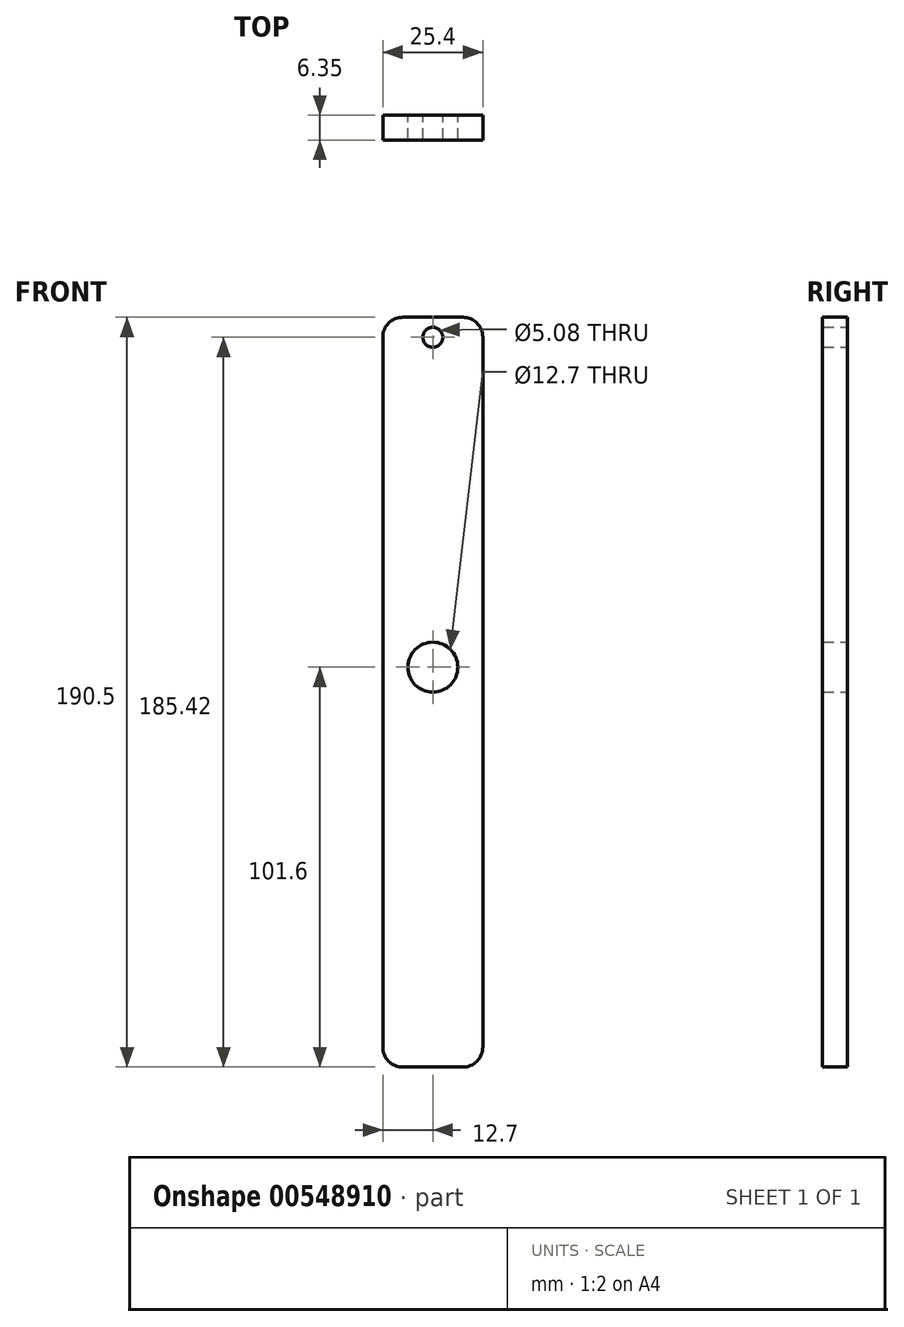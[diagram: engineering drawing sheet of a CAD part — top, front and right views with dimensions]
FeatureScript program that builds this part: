
annotation { "Feature Type Name" : "Feature", "Feature Type Description" : "" }
export const myFeature = defineFeature(function(context is Context, id is Id, definition is map)
    precondition{}
    {
        {
            var Q0;
            Q0=qCreatedBy(makeId("Front.planeOp"),FACE);
            var sketch = newSketch(context, id + "F0", { "sketchPlane" : qUnion([Q0])});
            skLineSegment(sketch, "E0.bottom", {"start": v(7.62, 95.25) * mm, "end": v(-7.62, 95.25) * mm});
            skLineSegment(sketch, "E0.top", {"start": v(7.62, -95.25) * mm, "end": v(-7.62, -95.25) * mm});
            skLineSegment(sketch, "E0.left", {"start": v(12.7, 90.17) * mm, "end": v(12.7, -90.17) * mm});
            skLineSegment(sketch, "E0.right", {"start": v(-12.7, 90.17) * mm, "end": v(-12.7, -90.17) * mm});
            skPoint(sketch, "E0.middle", {"position": v(0, 0) * mm});
            skLineSegment(sketch, "E1", {"start": v(0, 95.25) * mm, "end": v(0, 6.35) * mm});
            skPoint(sketch, "E1.endSnap0", {"position": v(0, 95.25) * mm});
            skCircle(sketch, "E2", {"center": v(0, 6.35) * mm, "radius": 6.35 * mm});
            skLineSegment(sketch, "E3", {"start": v(0, 95.25) * mm, "end": v(0, 90.17) * mm});
            skCircle(sketch, "E4", {"center": v(0, 90.17) * mm, "radius": 2.54 * mm});
            skPoint(sketch, "E5.visualSharp", {"position": v(-12.7, 95.25) * mm});
            skArc(sketch, "E5.filletArc", {"start": v(-7.62, 95.25) * mm, "mid": v(-11.21, 93.76) * mm, "end": v(-12.7, 90.17) * mm});
            skPoint(sketch, "E6.visualSharp", {"position": v(12.7, 95.25) * mm});
            skArc(sketch, "E6.filletArc", {"start": v(12.7, 90.17) * mm, "mid": v(11.21, 93.76) * mm, "end": v(7.62, 95.25) * mm});
            skPoint(sketch, "E7.visualSharp", {"position": v(-12.7, -95.25) * mm});
            skArc(sketch, "E7.filletArc", {"start": v(-12.7, -90.17) * mm, "mid": v(-11.21, -93.76) * mm, "end": v(-7.62, -95.25) * mm});
            skPoint(sketch, "E8.visualSharp", {"position": v(12.7, -95.25) * mm});
            skArc(sketch, "E8.filletArc", {"start": v(7.62, -95.25) * mm, "mid": v(11.21, -93.76) * mm, "end": v(12.7, -90.17) * mm});
            skSolve(sketch);
        }
        {
            var Q0;
            Q0=makeQuery(id+"F0.imprint","IMPRINT",FACE,{"disambiguationData":[TD([[makeQuery(id+"F0.imprint","IMPRINT",EDGE,{"derivedFrom":sQuery(id+"F0.wireOp",EDGE,"E0.top")}),-1.0]])]});
            extrude(context, id + "F1", {"entities" : qUnion([Q0]), "depth" : 6.35 * mm, "offsetDistance" : 25.4 * mm});
        }
    });
